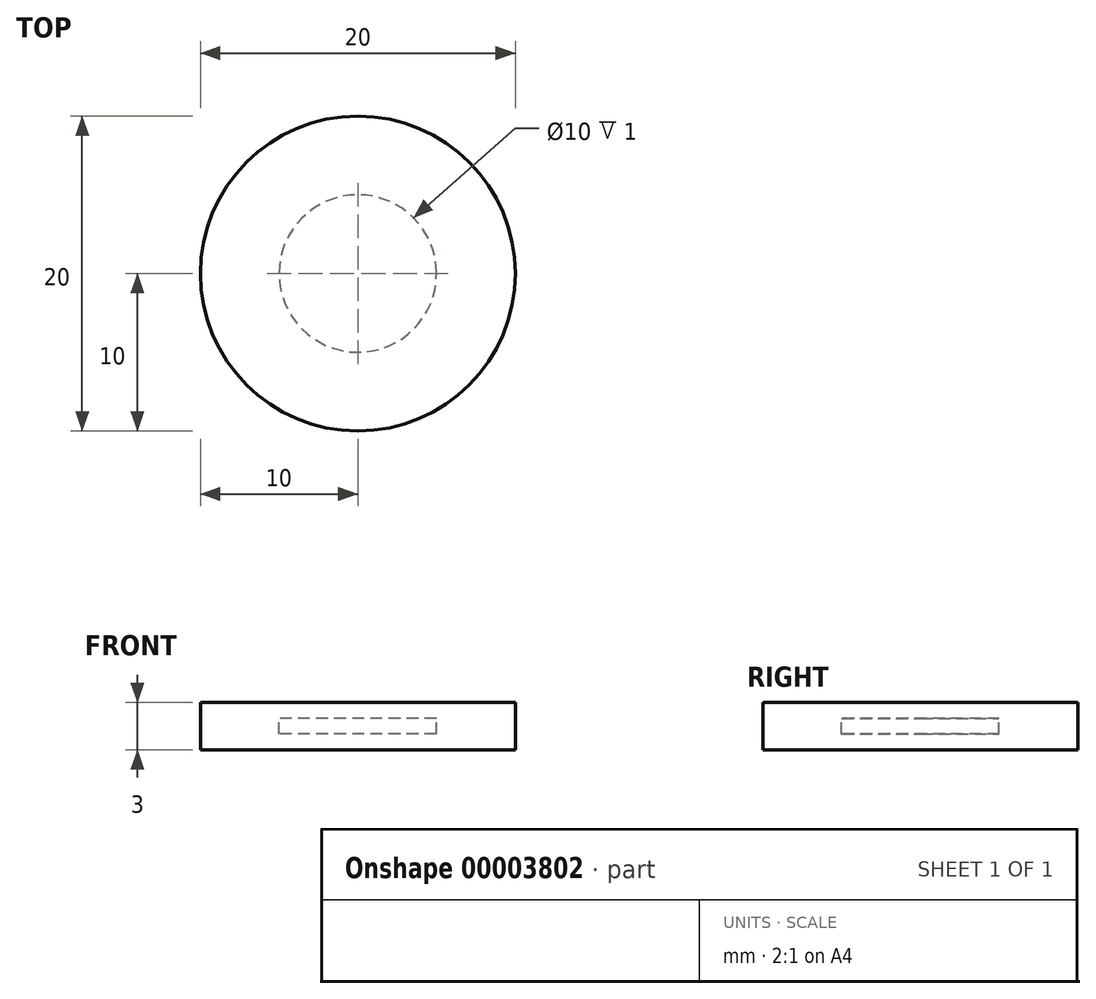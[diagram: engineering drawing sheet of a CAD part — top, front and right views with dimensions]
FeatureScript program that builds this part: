
annotation { "Feature Type Name" : "Feature", "Feature Type Description" : "" }
export const myFeature = defineFeature(function(context is Context, id is Id, definition is map)
    precondition{}
    {
        {
            var Q0;
            Q0=qCreatedBy(makeId("Top.planeOp"),FACE);
            var sketch = newSketch(context, id + "F0", { "sketchPlane" : qUnion([Q0])});
            skCircle(sketch, "E0", {"center": v(0, 0) * mm, "radius": 10 * mm});
            skSolve(sketch);
        }
        {
            var Q0;
            Q0 = qSketchRegion(id + "F0", true);
            extrude(context, id + "F1", {"entities" : qUnion([Q0]), "depth" : 2 * mm});
        }
        {
            var Q0;
            Q0=makeQuery(id+"F1.opExtrude","CAP_FACE",FACE,{"disambiguationData":[OSD([sQuery(id+"F0.wireOp",EDGE,"E0")])],"isStart":false});
            var sketch = newSketch(context, id + "F2", { "sketchPlane" : qUnion([Q0])});
            skCircle(sketch, "E1", {"center": v(0, 0) * mm, "radius": 5 * mm});
            skSolve(sketch);
        }
        {
            var Q0;
            Q0 = qSketchRegion(id + "F2", true);
            extrude(context, id + "F3", {"entities" : qUnion([Q0]), "operationType" : NewBodyOperationType.REMOVE, "oppositeDirection" : true, "depth" : 1 * mm});
        }
        {
            var Q0;
            Q0=makeQuery(id+"F1.opExtrude","CAP_FACE",FACE,{"disambiguationData":[OSD([sQuery(id+"F0.wireOp",EDGE,"E0")])],"isStart":false});
            var sketch = newSketch(context, id + "F4", { "sketchPlane" : qUnion([Q0])});
            skCircle(sketch, "E2.0", {"center": v(0, 0) * mm, "radius": 10 * mm});
            skSolve(sketch);
        }
        {
            var Q0;
            Q0 = qSketchRegion(id + "F4", true);
            extrude(context, id + "F5", {"entities" : qUnion([Q0]), "operationType" : NewBodyOperationType.ADD, "depth" : 1 * mm});
        }
    });
